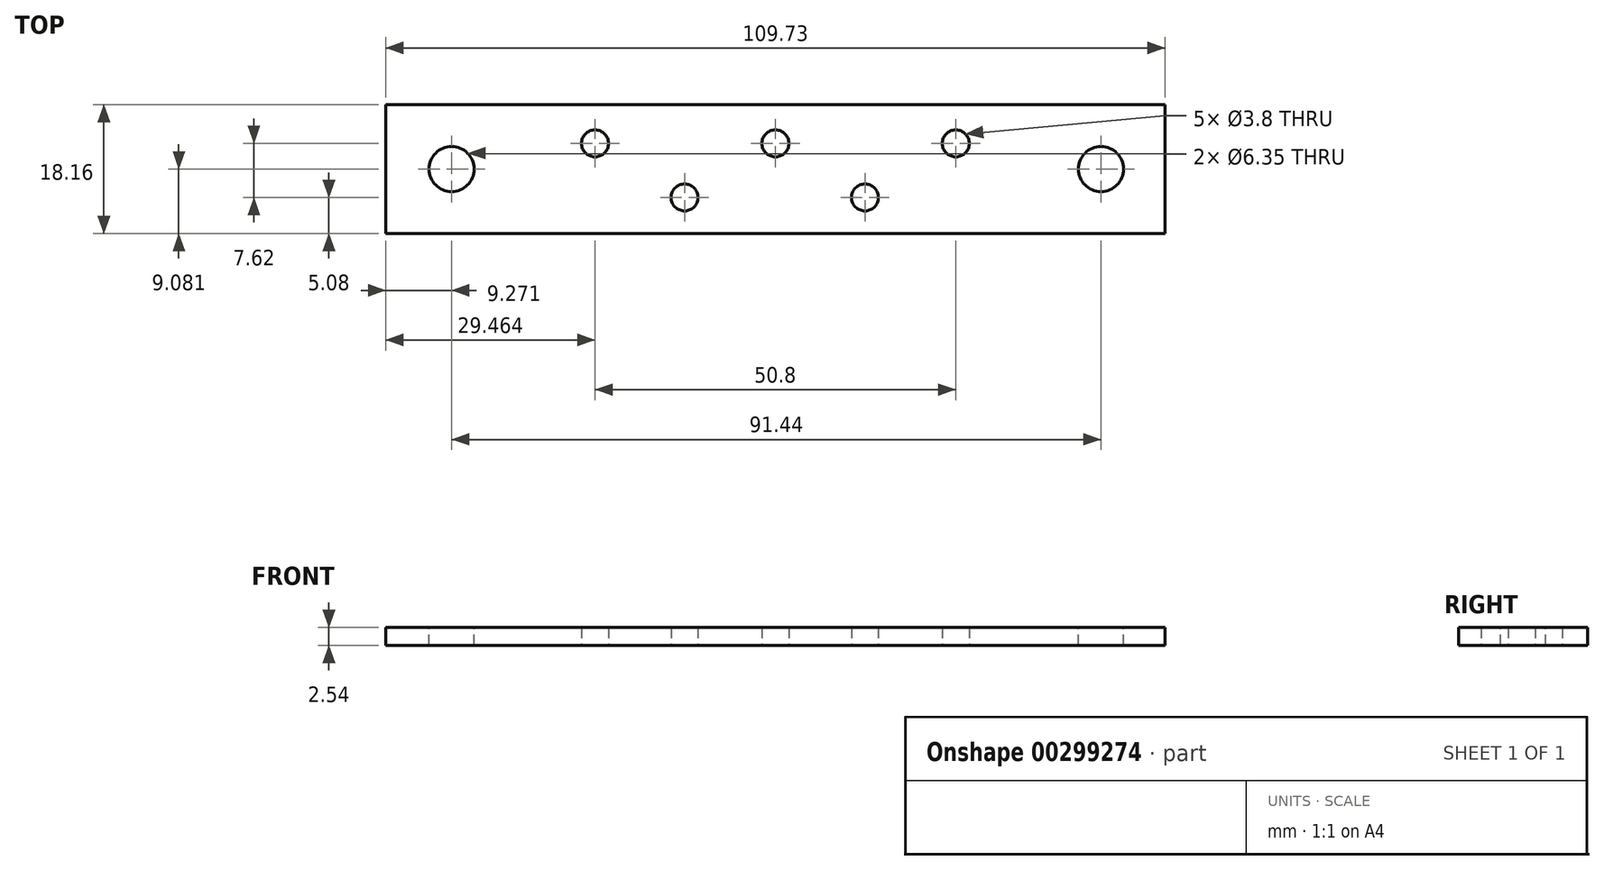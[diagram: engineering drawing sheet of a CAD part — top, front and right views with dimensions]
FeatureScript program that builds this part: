
annotation { "Feature Type Name" : "Feature", "Feature Type Description" : "" }
export const myFeature = defineFeature(function(context is Context, id is Id, definition is map)
    precondition{}
    {
        {
            var Q0;
            Q0=qCreatedBy(makeId("Top.planeOp"),FACE);
            var sketch = newSketch(context, id + "F0", { "sketchPlane" : qUnion([Q0])});
            skLineSegment(sketch, "E0.bottom", {"start": v(0, 0) * mm, "end": v(109.73, 0) * mm});
            skLineSegment(sketch, "E0.top", {"start": v(0, 18.16) * mm, "end": v(109.73, 18.16) * mm});
            skLineSegment(sketch, "E0.left", {"start": v(0, 0) * mm, "end": v(0, 18.16) * mm});
            skLineSegment(sketch, "E0.right", {"start": v(109.73, 0) * mm, "end": v(109.73, 18.16) * mm});
            skSolve(sketch);
        }
        {
            var Q0;
            Q0 = qSketchRegion(id + "F0", true);
            extrude(context, id + "F1", {"entities" : qUnion([Q0]), "depth" : 2.54 * mm});
        }
        {
            var Q0;
            Q0=makeQuery(id+"F1.opExtrude","CAP_FACE",FACE,{"disambiguationData":[OSD([sQuery(id+"F0.wireOp",EDGE,"E0.bottom"),sQuery(id+"F0.wireOp",EDGE,"E0.top"),sQuery(id+"F0.wireOp",EDGE,"E0.left"),sQuery(id+"F0.wireOp",EDGE,"E0.right")])],"isStart":false});
            var sketch = newSketch(context, id + "F2", { "sketchPlane" : qUnion([Q0])});
            skCircle(sketch, "E1", {"center": v(9.27, 9.08) * mm, "radius": 3.18 * mm});
            skCircle(sketch, "E2", {"center": v(100.71, 9.08) * mm, "radius": 3.18 * mm});
            skLineSegment(sketch, "E3", {"start": v(0, 9.08) * mm, "end": v(9.27, 9.08) * mm, "construction": true});
            skSolve(sketch);
        }
        {
            var Q0;
            Q0 = qSketchRegion(id + "F2", true);
            extrude(context, id + "F3", {"entities" : qUnion([Q0]), "operationType" : NewBodyOperationType.REMOVE, "endBound" : BoundingType.THROUGH_ALL, "oppositeDirection" : true, "depth" : 25.4 * mm});
        }
        {
            var Q0;
            Q0=makeQuery(id+"F1.opExtrude","CAP_FACE",FACE,{"disambiguationData":[OSD([sQuery(id+"F0.wireOp",EDGE,"E0.bottom"),sQuery(id+"F0.wireOp",EDGE,"E0.top"),sQuery(id+"F0.wireOp",EDGE,"E0.left"),sQuery(id+"F0.wireOp",EDGE,"E0.right")])],"isStart":false});
            var sketch = newSketch(context, id + "F4", { "sketchPlane" : qUnion([Q0])});
            skPoint(sketch, "E4", {"position": v(29.46, 12.7) * mm});
            skPoint(sketch, "E5", {"position": v(42.07, 5.08) * mm});
            skPoint(sketch, "E6", {"position": v(54.86, 12.7) * mm});
            skPoint(sketch, "E7", {"position": v(67.47, 5.08) * mm});
            skPoint(sketch, "E8", {"position": v(80.26, 12.7) * mm});
            skLineSegment(sketch, "E9", {"start": v(54.86, 0) * mm, "end": v(54.86, 12.7) * mm, "construction": true});
            skSolve(sketch);
        }
        {
            var Q0;
            Q0=sQuery(id+"F4.wireOp",VERTEX,"E4");
            var Q1;
            Q1=sQuery(id+"F4.wireOp",VERTEX,"E5");
            var Q2;
            Q2=sQuery(id+"F4.wireOp",VERTEX,"E6");
            var Q3;
            Q3=sQuery(id+"F4.wireOp",VERTEX,"E7");
            var Q4;
            Q4=sQuery(id+"F4.wireOp",VERTEX,"E8");
            var Q5;
            Q5=makeQuery(id+"F1.opExtrude","SWEPT_BODY",BODY,{"disambiguationData":[OSD([sQuery(id+"F0.wireOp",EDGE,"E0.bottom"),sQuery(id+"F0.wireOp",EDGE,"E0.top"),sQuery(id+"F0.wireOp",EDGE,"E0.left"),sQuery(id+"F0.wireOp",EDGE,"E0.right")])]});
            hole(context, id + "F5", {"style" : HoleStyle.SIMPLE, "endStyle" : HoleEndStyle.THROUGH, "standardTappedOrClearance" : lookupTablePath({ "standard" : "ANSI", "engagement" : "75%", "pitch" : "24 tpi", "size" : "#10", "type" : "Tapped" }), "standardBlindInLast" : lookupTablePath({ "standard" : "ANSI", "engagement" : "75%", "pitch" : "24 tpi", "size" : "#10", "type" : "Tapped" }), "holeDiameter" : 3.8 * mm, "showTappedDepth" : true, "isTappedThrough" : true, "tappedDepth" : 2.77 * mm, "tapClearance" : 3, "startFromSketch" : true, "locations" : qUnion([Q0, Q1, Q2, Q3, Q4]), "scope" : qUnion([Q5]), "majorDiameter" : 4.83 * mm});
        }
    });
